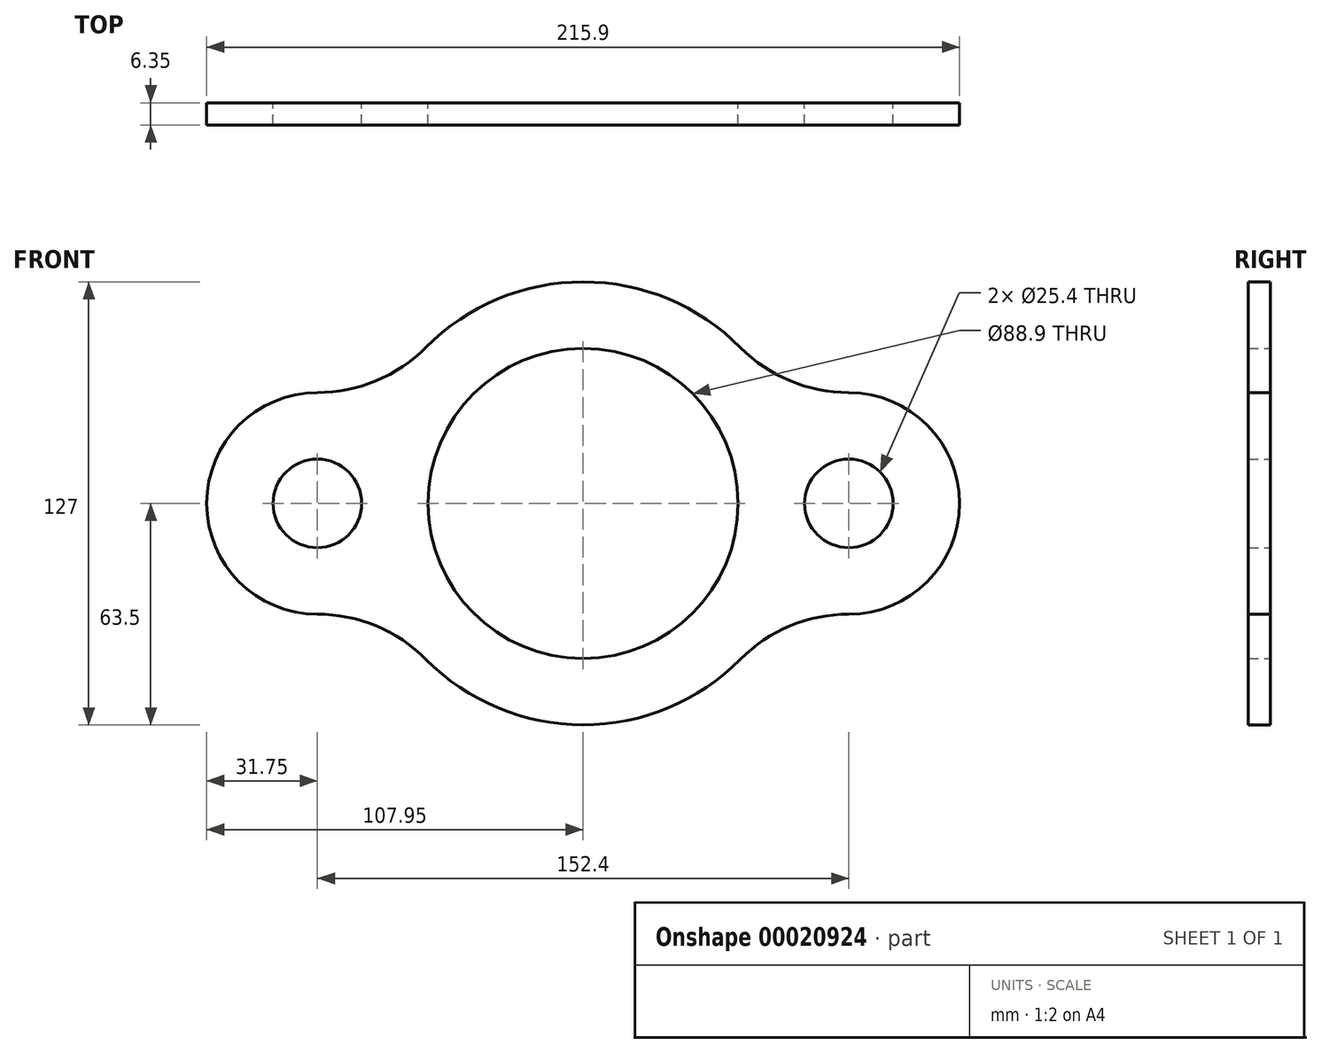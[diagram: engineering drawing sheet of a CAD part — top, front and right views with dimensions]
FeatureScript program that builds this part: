
annotation { "Feature Type Name" : "Feature", "Feature Type Description" : "" }
export const myFeature = defineFeature(function(context is Context, id is Id, definition is map)
    precondition{}
    {
        {
            var Q0;
            Q0=qCreatedBy(makeId("Front.planeOp"),FACE);
            var sketch = newSketch(context, id + "F0", { "sketchPlane" : qUnion([Q0])});
            skCircle(sketch, "E0", {"center": v(0, 0) * mm, "radius": 44.45 * mm});
            skCircle(sketch, "E1", {"center": v(-76.2, 0) * mm, "radius": 12.7 * mm});
            skCircle(sketch, "E2", {"center": v(76.2, 0) * mm, "radius": 12.7 * mm});
            skArc(sketch, "E3", {"start": v(-76.2, 31.75) * mm, "mid": v(-107.95, 0) * mm, "end": v(-76.2, -31.75) * mm});
            skArc(sketch, "E4", {"start": v(76.2, -31.75) * mm, "mid": v(107.95, 0) * mm, "end": v(76.2, 31.75) * mm});
            skArc(sketch, "E5", {"start": v(-45.09, -44.71) * mm, "mid": v(0, -63.5) * mm, "end": v(45.09, -44.71) * mm});
            skArc(sketch, "E6", {"start": v(-76.2, 31.75) * mm, "mid": v(-59.35, 35.12) * mm, "end": v(-45.09, 44.71) * mm});
            skArc(sketch, "E7", {"start": v(-45.09, -44.71) * mm, "mid": v(-59.35, -35.12) * mm, "end": v(-76.2, -31.75) * mm});
            skArc(sketch, "E8", {"start": v(76.2, -31.75) * mm, "mid": v(59.35, -35.12) * mm, "end": v(45.09, -44.71) * mm});
            skArc(sketch, "E9", {"start": v(45.09, 44.71) * mm, "mid": v(59.35, 35.12) * mm, "end": v(76.2, 31.75) * mm});
            skArc(sketch, "E10.trimOffspring", {"start": v(45.09, 44.71) * mm, "mid": v(0, 63.5) * mm, "end": v(-45.09, 44.71) * mm});
            skSolve(sketch);
        }
        {
            var Q0;
            Q0=makeQuery(id+"F0.imprint","IMPRINT",FACE,{"disambiguationData":[TD([[makeQuery(id+"F0.imprint","IMPRINT",EDGE,{"derivedFrom":sQuery(id+"F0.wireOp",EDGE,"E0")}),-1.0]])]});
            extrude(context, id + "F1", {"entities" : qUnion([Q0]), "depth" : 6.35 * mm});
        }
    });
